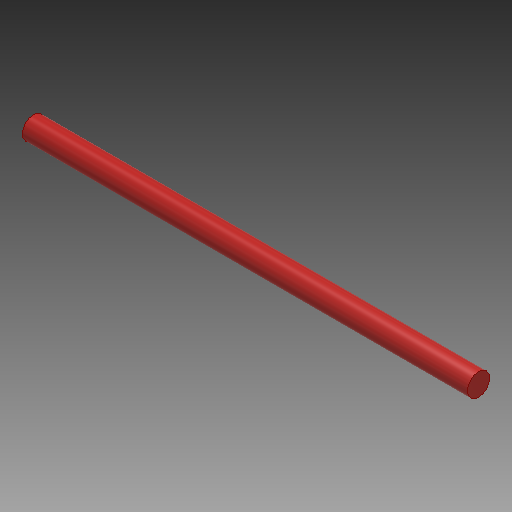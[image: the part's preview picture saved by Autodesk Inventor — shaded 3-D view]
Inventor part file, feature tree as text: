
AUTODESK INVENTOR PART (.ipt)
format: ipt  version: 2018.1 (Build 221171000, 171)  size: 95,232 bytes
history: native  units: mm
features: sketch x2, other x1, extrude x1
ambient origin geometry x8: Origin, YZ Plane, XZ Plane, XY Plane, X Axis, Y Axis, Z Axis, Center Point
bodies: Body1 (feature_tree)
feature tree (4):
  other  "ソリッド1"
  sketch  "スケッチ1"
  extrude  "押し出し1"  Depth=10.0mm
  sketch  "スケッチ2"
